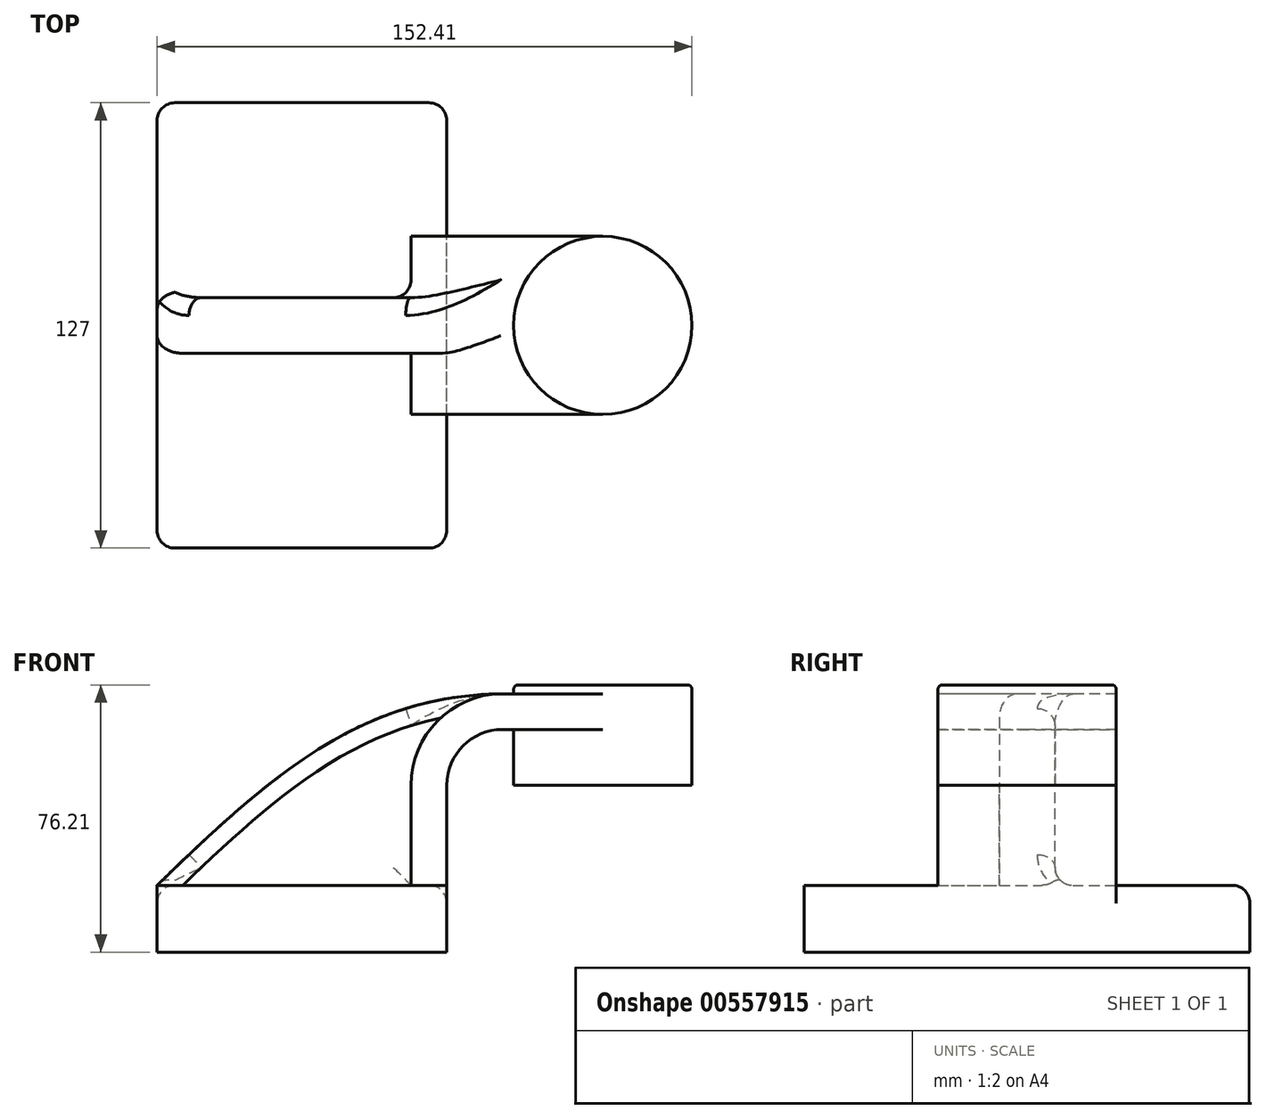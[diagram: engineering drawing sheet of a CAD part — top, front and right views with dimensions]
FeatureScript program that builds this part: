
annotation { "Feature Type Name" : "Feature", "Feature Type Description" : "" }
export const myFeature = defineFeature(function(context is Context, id is Id, definition is map)
    precondition{}
    {
        {
            var Q0;
            Q0=qCreatedBy(makeId("Front.planeOp"),FACE);
            var sketch = newSketch(context, id + "F0", { "sketchPlane" : qUnion([Q0])});
            skLineSegment(sketch, "E0.bottom", {"start": v(-41.27, -9.53) * mm, "end": v(41.28, -9.53) * mm});
            skLineSegment(sketch, "E0.top", {"start": v(-41.28, 9.53) * mm, "end": v(41.28, 9.53) * mm});
            skLineSegment(sketch, "E0.left", {"start": v(-41.28, -9.53) * mm, "end": v(-41.28, 9.53) * mm});
            skLineSegment(sketch, "E0.right", {"start": v(41.28, -9.53) * mm, "end": v(41.28, 9.53) * mm});
            skPoint(sketch, "E0.middle", {"position": v(0, 0) * mm});
            skLineSegment(sketch, "E1.bottom", {"start": v(60.32, 66.67) * mm, "end": v(111.12, 66.67) * mm});
            skLineSegment(sketch, "E1.top", {"start": v(60.33, 38.1) * mm, "end": v(111.12, 38.1) * mm});
            skLineSegment(sketch, "E1.left", {"start": v(60.32, 66.67) * mm, "end": v(60.33, 38.1) * mm});
            skLineSegment(sketch, "E1.right", {"start": v(111.12, 66.67) * mm, "end": v(111.12, 38.1) * mm});
            skPoint(sketch, "E1.middle", {"position": v(85.72, 52.39) * mm});
            skLineSegment(sketch, "E2", {"start": v(41.27, 9.53) * mm, "end": v(41.27, 38.1) * mm});
            skArc(sketch, "E3", {"start": v(41.27, 38.1) * mm, "mid": v(45.92, 49.33) * mm, "end": v(57.15, 53.97) * mm});
            skLineSegment(sketch, "E4", {"start": v(57.15, 53.97) * mm, "end": v(85.72, 53.97) * mm});
            skLineSegment(sketch, "E5.0", {"start": v(57.15, 64.13) * mm, "end": v(85.72, 64.13) * mm});
            skArc(sketch, "E5.1", {"start": v(31.11, 38.1) * mm, "mid": v(38.74, 56.5) * mm, "end": v(57.15, 64.13) * mm});
            skLineSegment(sketch, "E5.2", {"start": v(31.11, 9.53) * mm, "end": v(31.11, 38.1) * mm});
            skLineSegment(sketch, "E6", {"start": v(85.72, 38.1) * mm, "end": v(85.72, 66.67) * mm});
            skFitSpline(sketch, "E7", {"points": [v(-41.27, 9.53) * mm, v(57.15, 64.13) * mm], "startDerivative": vector(94.92, 92.43) * mm, "endDerivative": vector(121.27, 0.9) * mm});
            skSolve(sketch);
        }
        {
            var Q0;
            Q0=makeQuery(id+"F0.imprint","IMPRINT",FACE,{"disambiguationData":[TD([[makeQuery(id+"F0.imprint","IMPRINT",EDGE,{"derivedFrom":sQuery(id+"F0.wireOp",EDGE,"E0.bottom")}),1.0]])]});
            extrude(context, id + "F1", {"entities" : qUnion([Q0]), "endBound" : BoundingType.SYMMETRIC, "depth" : 127 * mm, "offsetDistance" : 25.4 * mm});
        }
        {
            var Q0;
            {var subQ1=sQuery(id+"F0.wireOp",EDGE,"E2");Q0=makeQuery(id+"F0.imprint","IMPRINT",FACE,{"disambiguationData":[TD([[makeQuery(id+"F0.imprint","IMPRINT",EDGE,{"derivedFrom":subQ1}),1.0]])]});}
            var Q1;
            {var subQ0=sQuery(id+"F0.wireOp",EDGE,"E5.0");var subQ1=sQuery(id+"F0.wireOp",EDGE,"E1.left");var subQ2=makeQuery(id+"F0.imprint","INTERSECT",VERTEX,{"derivedFrom":[subQ1,subQ0]});Q1=makeQuery(id+"F0.imprint","IMPRINT",FACE,{"disambiguationData":[TD([[makeQuery(id+"F0.imprint","IMPRINT",EDGE,{"disambiguationData":[TD([[subQ2,-1.0]])],"derivedFrom":subQ1}),1.0]])]});}
            extrude(context, id + "F2", {"entities" : qUnion([Q0, Q1]), "operationType" : NewBodyOperationType.ADD, "endBound" : BoundingType.SYMMETRIC, "depth" : 50.8 * mm, "offsetDistance" : 25.4 * mm});
        }
        {
            var Q0;
            {var subQ3=sQuery(id+"F0.wireOp",EDGE,"E5.2");Q0=makeQuery(id+"F0.imprint","IMPRINT",FACE,{"disambiguationData":[TD([[makeQuery(id+"F0.imprint","IMPRINT",EDGE,{"derivedFrom":subQ3}),1.0]])]});}
            extrude(context, id + "F3", {"entities" : qUnion([Q0]), "operationType" : NewBodyOperationType.ADD, "endBound" : BoundingType.SYMMETRIC, "depth" : 15.88 * mm, "offsetDistance" : 25.4 * mm});
        }
        {
            var Q0;
            {var subQ4=sQuery(id+"F0.wireOp",EDGE,"E1.right");Q0=makeQuery(id+"F0.imprint","IMPRINT",FACE,{"disambiguationData":[TD([[makeQuery(id+"F0.imprint","IMPRINT",EDGE,{"derivedFrom":subQ4}),-1.0]])]});}
            var Q1;
            Q1=sQuery(id+"F0.wireOp",EDGE,"E6");
            revolve(context, id + "F4", {"operationType" : NewBodyOperationType.ADD, "entities" : qUnion([Q0]), "axis" : qUnion([Q1]), "revolveType" : RevolveType.FULL});
        }
        {
            var Q0;
            Q0=makeQuery(id+"F1.opExtrude","CAP_EDGE",EDGE,{"disambiguationData":[OSD([sQuery(id+"F0.wireOp",EDGE,"E0.right")])],"isStart":false});
            var Q1;
            Q1=makeQuery(id+"F1.opExtrude","CAP_EDGE",EDGE,{"disambiguationData":[OSD([sQuery(id+"F0.wireOp",EDGE,"E0.left")])],"isStart":false});
            var Q2;
            Q2=makeQuery(id+"F1.opExtrude","CAP_EDGE",EDGE,{"disambiguationData":[OSD([sQuery(id+"F0.wireOp",EDGE,"E0.right")])],"isStart":true});
            var Q3;
            Q3=makeQuery(id+"F1.opExtrude","CAP_EDGE",EDGE,{"disambiguationData":[OSD([sQuery(id+"F0.wireOp",EDGE,"E0.left")])],"isStart":true});
            fillet(context, id + "F5", {"entities" : qUnion([Q0, Q1, Q2, Q3]), "radius" : 5.08 * mm, "tangentPropagation" : true, "allowEdgeOverflow" : false});
        }
        {
            var Q0;
            Q0=makeQuery(id+"F4.opRevolve","SWEPT_EDGE",EDGE,{"disambiguationData":[OSD([sQuery(id+"F0.wireOp",EDGE,"E1.bottom"),sQuery(id+"F0.wireOp",EDGE,"E1.right")])]});
            fillet(context, id + "F6", {"entities" : qUnion([Q0]), "radius" : 1.27 * mm, "tangentPropagation" : true, "allowEdgeOverflow" : false});
        }
        {
            var Q0;
            Q0=makeQuery(id+"F3.opExtrude","CAP_EDGE",EDGE,{"disambiguationData":[OSD([sQuery(id+"F0.wireOp",EDGE,"E0.top")])],"isStart":true});
            var Q1;
            Q1=makeQuery(id+"F3.opExtrude","CAP_EDGE",EDGE,{"disambiguationData":[OSD([sQuery(id+"F0.wireOp",EDGE,"E0.top")])],"isStart":false});
            var Q2;
            Q2=makeQuery(id+"F3.opExtrude","CAP_EDGE",EDGE,{"disambiguationData":[OSD([sQuery(id+"F0.wireOp",EDGE,"E5.2")])],"isStart":false});
            var Q3;
            Q3=makeQuery(id+"F3.opExtrude","CAP_EDGE",EDGE,{"disambiguationData":[OSD([sQuery(id+"F0.wireOp",EDGE,"E5.2")])],"isStart":true});
            fillet(context, id + "F7", {"entities" : qUnion([Q0, Q1, Q2, Q3]), "radius" : 5.08 * mm, "tangentPropagation" : true, "allowEdgeOverflow" : false});
        }
        {
            var Q0;
            Q0=makeQuery(id+"F3.opExtrude","CAP_EDGE",EDGE,{"disambiguationData":[OSD([sQuery(id+"F0.wireOp",EDGE,"E7")])],"isStart":false});
            var Q1;
            Q1=makeQuery(id+"F3.opExtrude","CAP_EDGE",EDGE,{"disambiguationData":[OSD([sQuery(id+"F0.wireOp",EDGE,"E7")])],"isStart":true});
            fillet(context, id + "F8", {"entities" : qUnion([Q0, Q1]), "radius" : 5.08 * mm, "tangentPropagation" : true, "allowEdgeOverflow" : false});
        }
    });
